FCSTD DOCUMENT  (FreeCAD 1.0R38641 +468 (Git))
Label: Upper_arm
License: All rights reserved
LicenseURL: https://en.wikipedia.org/wiki/All_rights_reserved
objects: App::Link×2, App::FeaturePython×1, Assembly::JointGroup×1, Assembly::AssemblyObject×1, App::Part×1, Mesh::Feature×1
EXTERNAL_REF file=M2.FCStd obj=M004
EXTERNAL_REF file=M1.FCStd obj=M003

FEATURE [App::Link] M004
  LinkPlacement = pos=(65.5953,-1.88612,-22.6499) rot=(0,0,1;0rad)
  LinkedObject = -> <external M2.FCStd>#M004
  Placement = pos=(65.5953,-1.88612,-22.6499) rot=(0,0,1;0rad)
FEATURE [App::FeaturePython] GroundedJoint  # Assembly grounded joint (typed FeaturePython)
  ObjectToGround = -> M004
  Placement = pos=(65.5953,-1.88612,-22.6499) rot=(0,0,1;0rad)
FEATURE [Assembly::JointGroup] Joints
  Group = -> [GroundedJoint]
FEATURE [App::Link] M003
  LinkPlacement = pos=(65.59,-1.89,-22.65) rot=(0,0,1;0rad)
  LinkedObject = -> <external M1.FCStd>#M003
  Placement = pos=(65.59,-1.89,-22.65) rot=(0,0,1;0rad)
FEATURE [Assembly::AssemblyObject] Assembly
  Group = -> [Joints,M004,GroundedJoint,M003]
  Origin = -> Origin
  Placement = pos=(99.5,0,179.5) rot=(-0.11,-0.13,-0.99;0rad)
  Type = Assembly
FEATURE [App::Part] Part
  Group = -> [Assembly]
  Origin = -> Origin001
  Placement = pos=(1.95,25.7,25.05) rot=(-0.57735,-0.57735,-0.57735;2.0944rad)
FEATURE [Mesh::Feature] Mesh  label="Part (Meshed)"

RESOLVED EXTERNAL PARTS (link-assembly join: the EXTERNAL_REF files above that resolve inside this repo's crawl, each included once):
---- part M1.FCStd = doc fcstd_caae7d9043dd ----
FCSTD DOCUMENT  (FreeCAD 1.0R38641 +468 (Git))
Label: M1
License: All rights reserved
LicenseURL: https://en.wikipedia.org/wiki/All_rights_reserved
objects: Mesh::Feature×1, Part::Feature×1, Part::Refine×1
note: 2 computed .brp shape members not serialized (recipe doc carries the construction recipe); baked Part::Feature solids carry a one-line shape summary decoded from their .brp

FEATURE [Mesh::Feature] M1
FEATURE [Part::Feature] M002
  shape: bbox 130 x 39.93 x 32.5 mm, 3768 faces, 0 solids (baked)
FEATURE [Part::Refine] M003
  Source = -> M002
---- part M2.FCStd = doc fcstd_422d414246c8 ----
FCSTD DOCUMENT  (FreeCAD 1.0R38641 +468 (Git))
Label: M2
License: All rights reserved
LicenseURL: https://en.wikipedia.org/wiki/All_rights_reserved
objects: Part::Feature×1, Part::Refine×1
note: 2 computed .brp shape members not serialized (recipe doc carries the construction recipe); baked Part::Feature solids carry a one-line shape summary decoded from their .brp

FEATURE [Part::Feature] M003
  shape: bbox 130 x 39.93 x 32.5 mm, 4246 faces, 0 solids (baked)
FEATURE [Part::Refine] M004
  Source = -> M003
